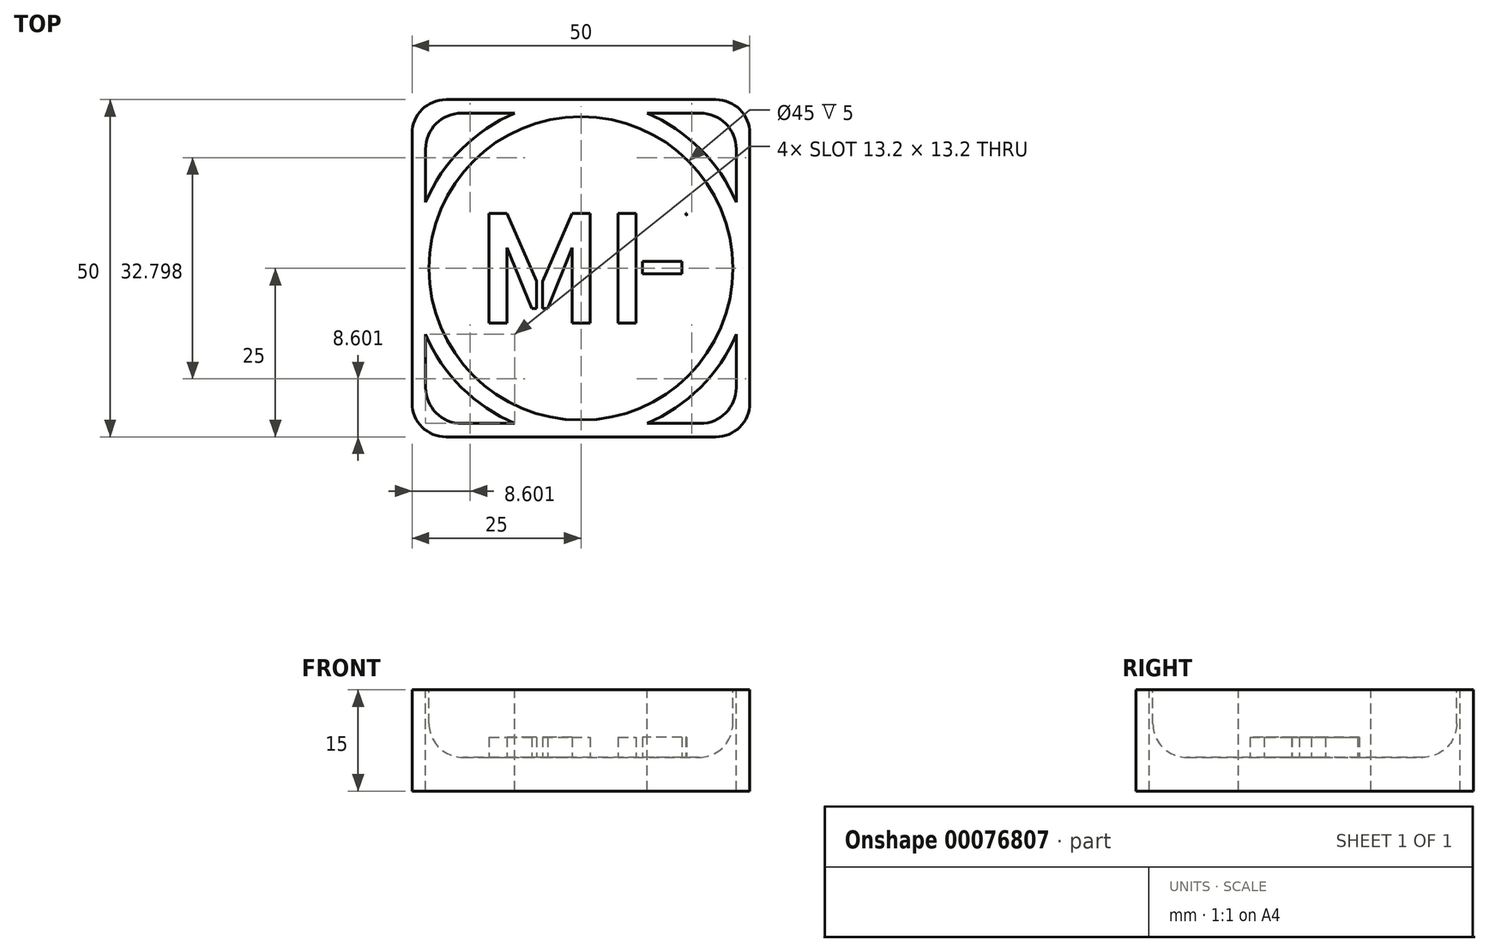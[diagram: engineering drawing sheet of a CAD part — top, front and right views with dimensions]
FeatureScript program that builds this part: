
annotation { "Feature Type Name" : "Feature", "Feature Type Description" : "" }
export const myFeature = defineFeature(function(context is Context, id is Id, definition is map)
    precondition{}
    {
        {
            var Q0;
            Q0=qCreatedBy(makeId("Top.planeOp"),FACE);
            var sketch = newSketch(context, id + "F0", { "sketchPlane" : qUnion([Q0])});
            skLineSegment(sketch, "E0.bottom", {"start": v(25, 25) * mm, "end": v(-25, 25) * mm});
            skLineSegment(sketch, "E0.top", {"start": v(25, -25) * mm, "end": v(-25, -25) * mm});
            skLineSegment(sketch, "E0.left", {"start": v(25, 25) * mm, "end": v(25, -25) * mm});
            skLineSegment(sketch, "E0.right", {"start": v(-25, 25) * mm, "end": v(-25, -25) * mm});
            skPoint(sketch, "E0.middle", {"position": v(0, 0) * mm});
            skSolve(sketch);
        }
        {
            var Q0;
            Q0=makeQuery(id+"F0.imprint","IMPRINT",FACE,{"disambiguationData":[TD([[makeQuery(id+"F0.imprint","IMPRINT",EDGE,{"derivedFrom":sQuery(id+"F0.wireOp",EDGE,"E0.bottom")}),1.0]])]});
            extrude(context, id + "F1", {"entities" : qUnion([Q0]), "depth" : 15 * mm});
        }
        {
            var Q0;
            Q0=makeQuery(id+"F1.opExtrude","SWEPT_EDGE",EDGE,{"disambiguationData":[OSD([sQuery(id+"F0.wireOp",EDGE,"E0.top"),sQuery(id+"F0.wireOp",EDGE,"E0.left")])]});
            var Q1;
            Q1=makeQuery(id+"F1.opExtrude","SWEPT_EDGE",EDGE,{"disambiguationData":[OSD([sQuery(id+"F0.wireOp",EDGE,"E0.top"),sQuery(id+"F0.wireOp",EDGE,"E0.right")])]});
            var Q2;
            Q2=makeQuery(id+"F1.opExtrude","SWEPT_EDGE",EDGE,{"disambiguationData":[OSD([sQuery(id+"F0.wireOp",EDGE,"E0.bottom"),sQuery(id+"F0.wireOp",EDGE,"E0.left")])]});
            var Q3;
            Q3=makeQuery(id+"F1.opExtrude","SWEPT_EDGE",EDGE,{"disambiguationData":[OSD([sQuery(id+"F0.wireOp",EDGE,"E0.bottom"),sQuery(id+"F0.wireOp",EDGE,"E0.right")])]});
            fillet(context, id + "F2", {"entities" : qUnion([Q0, Q1, Q2, Q3]), "radius" : 5 * mm, "tangentPropagation" : true, "allowEdgeOverflow" : false});
        }
        {
            var Q0;
            Q0=makeQuery(id+"F1.opExtrude","CAP_FACE",FACE,{"disambiguationData":[OSD([sQuery(id+"F0.wireOp",EDGE,"E0.bottom"),sQuery(id+"F0.wireOp",EDGE,"E0.top"),sQuery(id+"F0.wireOp",EDGE,"E0.left"),sQuery(id+"F0.wireOp",EDGE,"E0.right")])],"isStart":false});
            var sketch = newSketch(context, id + "F3", { "sketchPlane" : qUnion([Q0])});
            skCircle(sketch, "E1", {"center": v(0, 0) * mm, "radius": 22.5 * mm});
            skSolve(sketch);
        }
        {
            var Q0;
            Q0=makeQuery(id+"F3.imprint","IMPRINT",FACE,{"disambiguationData":[TD([[makeQuery(id+"F3.imprint","IMPRINT",EDGE,{"derivedFrom":sQuery(id+"F3.wireOp",EDGE,"E1")}),1.0]])]});
            extrude(context, id + "F4", {"entities" : qUnion([Q0]), "operationType" : NewBodyOperationType.REMOVE, "oppositeDirection" : true, "depth" : 10 * mm});
        }
        {
            var Q0;
            Q0=makeQuery(id+"F4.boolean.opBoolean","COPY",EDGE,{"derivedFrom":makeQuery(id+"F4.opExtrude","CAP_EDGE",EDGE,{"disambiguationData":[OSD([sQuery(id+"F3.wireOp",EDGE,"E1")])],"isStart":false})});
            fillet(context, id + "F5", {"entities" : qUnion([Q0]), "radius" : 5 * mm, "tangentPropagation" : true, "allowEdgeOverflow" : false});
        }
        {
            var Q0;
            Q0=makeQuery(id+"F1.opExtrude","CAP_FACE",FACE,{"disambiguationData":[OSD([sQuery(id+"F0.wireOp",EDGE,"E0.bottom"),sQuery(id+"F0.wireOp",EDGE,"E0.top"),sQuery(id+"F0.wireOp",EDGE,"E0.left"),sQuery(id+"F0.wireOp",EDGE,"E0.right")])],"isStart":false});
            var sketch = newSketch(context, id + "F6", { "sketchPlane" : qUnion([Q0])});
            skLineSegment(sketch, "E2", {"start": v(-14.75, -23) * mm, "end": v(-9.8, -23) * mm});
            skLineSegment(sketch, "E3", {"start": v(-23, -15.77) * mm, "end": v(-23, -9.8) * mm});
            skArc(sketch, "E4", {"start": v(-17.68, -23) * mm, "mid": v(-21.44, -21.44) * mm, "end": v(-23, -17.68) * mm});
            skLineSegment(sketch, "E5", {"start": v(-14.75, -23) * mm, "end": v(-17.68, -23) * mm});
            skLineSegment(sketch, "E6", {"start": v(-23, -17.68) * mm, "end": v(-23, -15.77) * mm});
            skArc(sketch, "E7", {"start": v(-9.8, -23) * mm, "mid": v(-17.68, -17.68) * mm, "end": v(-23, -9.8) * mm});
            skArc(sketch, "E8.1.0", {"start": v(23, -9.8) * mm, "mid": v(17.68, -17.68) * mm, "end": v(9.8, -23) * mm});
            skLineSegment(sketch, "E8.1.1", {"start": v(15.77, -23) * mm, "end": v(9.8, -23) * mm});
            skLineSegment(sketch, "E8.1.2", {"start": v(17.68, -23) * mm, "end": v(15.77, -23) * mm});
            skArc(sketch, "E8.1.3", {"start": v(23, -17.68) * mm, "mid": v(21.44, -21.44) * mm, "end": v(17.68, -23) * mm});
            skLineSegment(sketch, "E8.1.4", {"start": v(23, -14.75) * mm, "end": v(23, -17.68) * mm});
            skLineSegment(sketch, "E8.1.5", {"start": v(23, -14.75) * mm, "end": v(23, -9.8) * mm});
            skArc(sketch, "E8.2.0", {"start": v(9.8, 23) * mm, "mid": v(17.68, 17.68) * mm, "end": v(23, 9.8) * mm});
            skLineSegment(sketch, "E8.2.1", {"start": v(23, 15.77) * mm, "end": v(23, 9.8) * mm});
            skLineSegment(sketch, "E8.2.2", {"start": v(23, 17.68) * mm, "end": v(23, 15.77) * mm});
            skArc(sketch, "E8.2.3", {"start": v(17.68, 23) * mm, "mid": v(21.44, 21.44) * mm, "end": v(23, 17.68) * mm});
            skLineSegment(sketch, "E8.2.4", {"start": v(14.75, 23) * mm, "end": v(17.68, 23) * mm});
            skLineSegment(sketch, "E8.2.5", {"start": v(14.75, 23) * mm, "end": v(9.8, 23) * mm});
            skArc(sketch, "E8.3.0", {"start": v(-23, 9.8) * mm, "mid": v(-17.68, 17.68) * mm, "end": v(-9.8, 23) * mm});
            skLineSegment(sketch, "E8.3.1", {"start": v(-15.77, 23) * mm, "end": v(-9.8, 23) * mm});
            skLineSegment(sketch, "E8.3.2", {"start": v(-17.68, 23) * mm, "end": v(-15.77, 23) * mm});
            skArc(sketch, "E8.3.3", {"start": v(-23, 17.68) * mm, "mid": v(-21.44, 21.44) * mm, "end": v(-17.68, 23) * mm});
            skLineSegment(sketch, "E8.3.4", {"start": v(-23, 14.75) * mm, "end": v(-23, 17.68) * mm});
            skLineSegment(sketch, "E8.3.5", {"start": v(-23, 14.75) * mm, "end": v(-23, 9.8) * mm});
            skSolve(sketch);
        }
        {
            var Q0;
            Q0 = qSketchRegion(id + "F6", true);
            extrude(context, id + "F7", {"entities" : qUnion([Q0]), "operationType" : NewBodyOperationType.REMOVE, "oppositeDirection" : true, "depth" : 25 * mm});
        }
        {
            var Q0;
            Q0=makeQuery(id+"F4.boolean.opBoolean","COPY",FACE,{"derivedFrom":makeQuery(id+"F4.opExtrude","CAP_FACE",FACE,{"disambiguationData":[OSD([sQuery(id+"F3.wireOp",EDGE,"E1")])],"isStart":false})});
            var sketch = newSketch(context, id + "F8", { "sketchPlane" : qUnion([Q0])});
            skText(sketch, "E9", { "text": "MF", "fontName": "AllertaStencil-Regular.ttf"});
            const initialGuessF8  = {"E9": [-0.01565, -0.00812, 1, 0, 0.01624]};
            skSetInitialGuess(sketch, initialGuessF8);
            skSolve(sketch);
        }
        {
            var Q0;
            Q0=makeQuery(id+"F8.imprint","IMPRINT",FACE,{"disambiguationData":[TD([[makeQuery(id+"F8.imprint","IMPRINT",EDGE,{"derivedFrom":sQuery(id+"F8.wireOp",EDGE,"E9.sketch_text.stroke-0")}),-1.0]])]});
            var Q1;
            Q1=makeQuery(id+"F8.imprint","IMPRINT",FACE,{"disambiguationData":[TD([[makeQuery(id+"F8.imprint","IMPRINT",EDGE,{"derivedFrom":sQuery(id+"F8.wireOp",EDGE,"E9.sketch_text.stroke-8")}),-1.0]])]});
            var Q2;
            Q2=makeQuery(id+"F8.imprint","IMPRINT",FACE,{"disambiguationData":[TD([[makeQuery(id+"F8.imprint","IMPRINT",EDGE,{"derivedFrom":sQuery(id+"F8.wireOp",EDGE,"E9.sketch_text.stroke-16")}),-1.0]])]});
            var Q3;
            Q3=makeQuery(id+"F8.imprint","IMPRINT",FACE,{"disambiguationData":[TD([[makeQuery(id+"F8.imprint","IMPRINT",EDGE,{"derivedFrom":sQuery(id+"F8.wireOp",EDGE,"E9.sketch_text.stroke-20")}),-1.0]])]});
            var Q4;
            Q4=makeQuery(id+"F8.imprint","IMPRINT",FACE,{"disambiguationData":[TD([[makeQuery(id+"F8.imprint","IMPRINT",EDGE,{"derivedFrom":sQuery(id+"F8.wireOp",EDGE,"E9.sketch_text.stroke-24")}),-1.0]])]});
            extrude(context, id + "F9", {"entities" : qUnion([Q0, Q1, Q2, Q3, Q4]), "operationType" : NewBodyOperationType.ADD, "depth" : 3 * mm});
        }
    });
